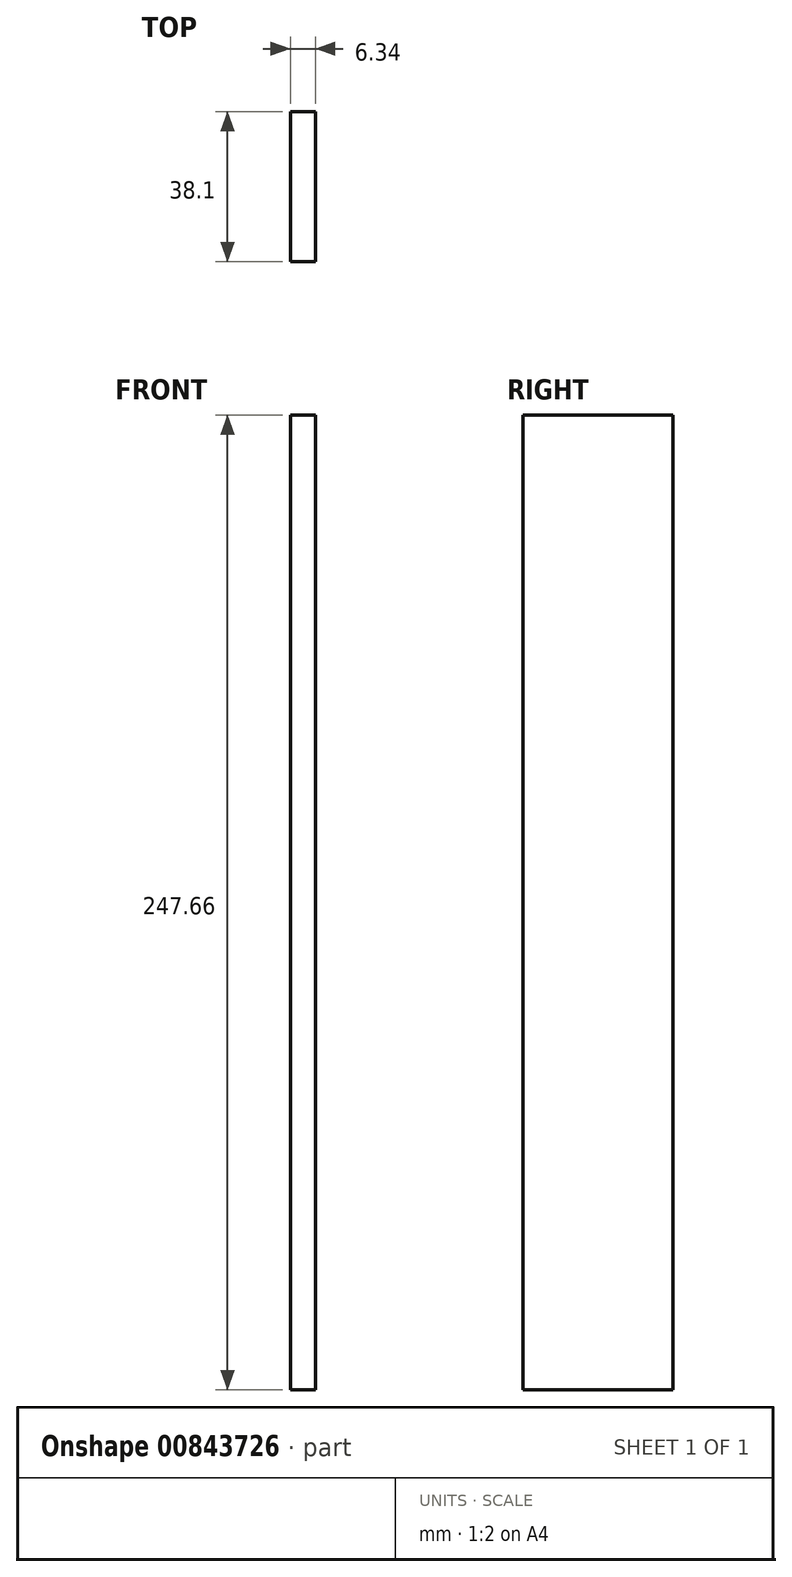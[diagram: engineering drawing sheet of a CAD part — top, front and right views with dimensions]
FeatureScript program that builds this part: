
annotation { "Feature Type Name" : "Feature", "Feature Type Description" : "" }
export const myFeature = defineFeature(function(context is Context, id is Id, definition is map)
    precondition{}
    {
        {
            var Q0;
            Q0=qCreatedBy(makeId("Front.planeOp"),FACE);
            var sketch = newSketch(context, id + "F0", { "sketchPlane" : qUnion([Q0])});
            skLineSegment(sketch, "E0.bottom", {"start": v(3.17, 123.83) * mm, "end": v(-3.18, 123.83) * mm});
            skLineSegment(sketch, "E0.top", {"start": v(3.18, -123.83) * mm, "end": v(-3.17, -123.83) * mm});
            skLineSegment(sketch, "E0.left", {"start": v(3.17, 123.83) * mm, "end": v(3.18, -123.83) * mm});
            skLineSegment(sketch, "E0.right", {"start": v(-3.18, 123.83) * mm, "end": v(-3.17, -123.83) * mm});
            skPoint(sketch, "E0.middle", {"position": v(0, 0) * mm});
            skSolve(sketch);
        }
        {
            var Q0;
            Q0 = qSketchRegion(id + "F0", true);
            extrude(context, id + "F1", {"entities" : qUnion([Q0]), "depth" : 38.1 * mm, "offsetDistance" : 25.4 * mm});
        }
    });
